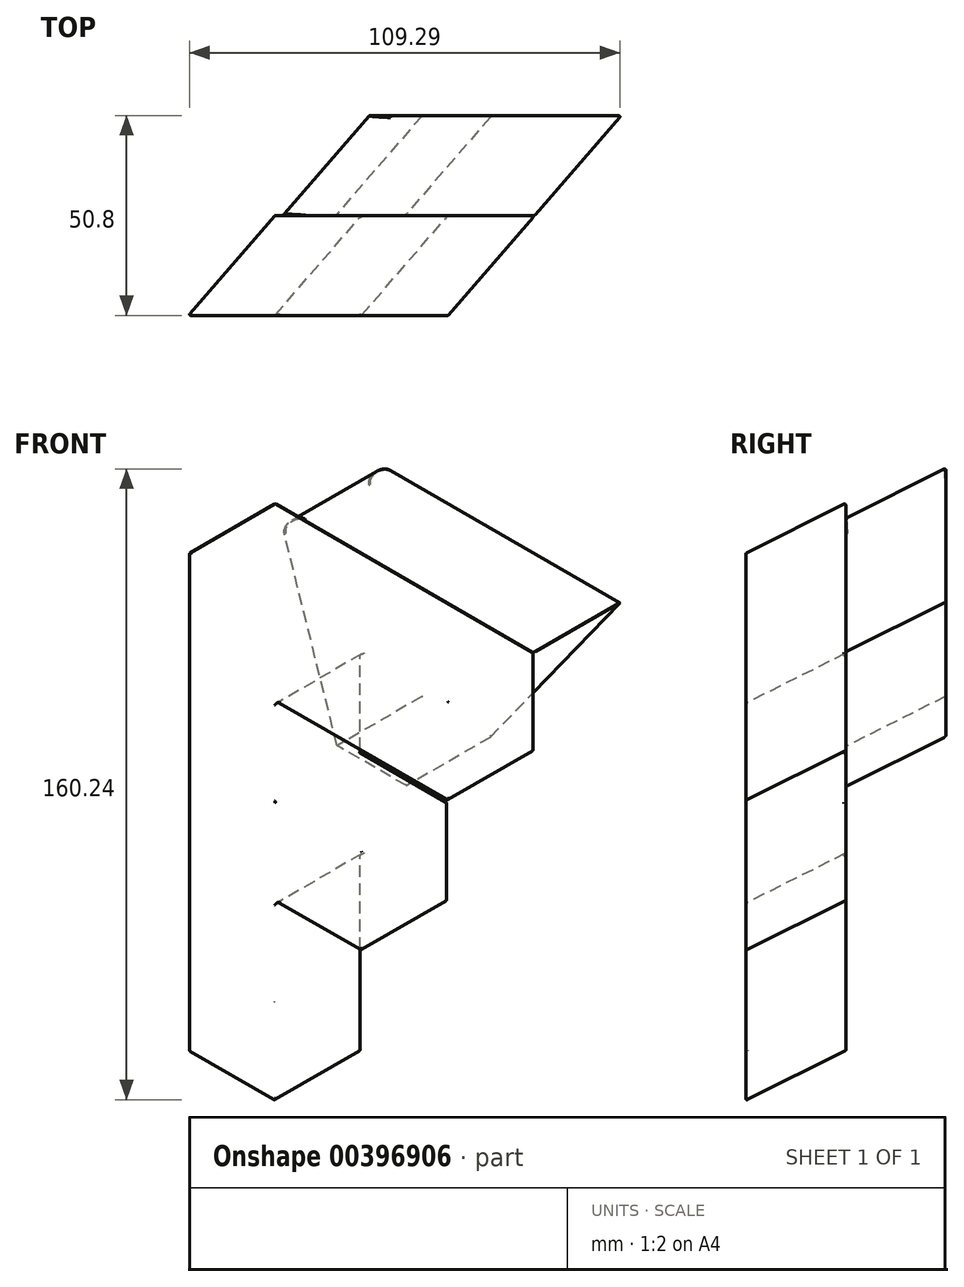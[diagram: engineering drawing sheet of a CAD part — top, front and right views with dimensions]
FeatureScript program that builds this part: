
annotation { "Feature Type Name" : "Feature", "Feature Type Description" : "" }
export const myFeature = defineFeature(function(context is Context, id is Id, definition is map)
    precondition{}
    {
        {
            var Q0;
            Q0=qCreatedBy(makeId("Front.planeOp"),FACE);
            var sketch = newSketch(context, id + "F0", { "sketchPlane" : qUnion([Q0])});
            skLineSegment(sketch, "E0", {"start": v(0, 0) * mm, "end": v(0, 127) * mm});
            skLineSegment(sketch, "E1", {"start": v(0, 127) * mm, "end": v(66, 88.9) * mm});
            skLineSegment(sketch, "E2", {"start": v(66, 88.9) * mm, "end": v(66, 63.5) * mm});
            skLineSegment(sketch, "E3", {"start": v(66, 63.5) * mm, "end": v(22, 88.9) * mm});
            skLineSegment(sketch, "E4", {"start": v(22, 88.9) * mm, "end": v(22, 63.5) * mm});
            skLineSegment(sketch, "E5", {"start": v(22, 63.5) * mm, "end": v(44, 50.8) * mm});
            skLineSegment(sketch, "E6", {"start": v(44, 50.8) * mm, "end": v(44, 25.4) * mm});
            skLineSegment(sketch, "E7", {"start": v(44, 25.4) * mm, "end": v(22, 38.1) * mm});
            skLineSegment(sketch, "E8", {"start": v(22, 38.1) * mm, "end": v(22, -12.7) * mm});
            skLineSegment(sketch, "E9", {"start": v(22, -12.7) * mm, "end": v(0, 0) * mm});
            skLineSegment(sketch, "E10", {"start": v(0, 0) * mm, "end": v(22, 12.7) * mm, "construction": true});
            skLineSegment(sketch, "E11", {"start": v(22, 12.7) * mm, "end": v(0, 25.4) * mm, "construction": true});
            skLineSegment(sketch, "E12", {"start": v(0, 25.4) * mm, "end": v(22, 38.1) * mm, "construction": true});
            skLineSegment(sketch, "E13", {"start": v(22, 38.1) * mm, "end": v(0, 50.8) * mm, "construction": true});
            skLineSegment(sketch, "E14", {"start": v(0, 50.8) * mm, "end": v(22, 63.5) * mm, "construction": true});
            skLineSegment(sketch, "E15", {"start": v(22, 63.5) * mm, "end": v(0, 76.2) * mm, "construction": true});
            skLineSegment(sketch, "E16", {"start": v(0, 76.2) * mm, "end": v(22, 88.9) * mm, "construction": true});
            skLineSegment(sketch, "E17", {"start": v(22, 88.9) * mm, "end": v(0, 101.6) * mm, "construction": true});
            skLineSegment(sketch, "E18", {"start": v(0, 101.6) * mm, "end": v(22, 114.3) * mm, "construction": true});
            skLineSegment(sketch, "E19", {"start": v(22, 38.1) * mm, "end": v(44, 50.8) * mm, "construction": true});
            skLineSegment(sketch, "E20", {"start": v(22, 88.9) * mm, "end": v(44, 101.6) * mm, "construction": true});
            skLineSegment(sketch, "E21", {"start": v(44, 101.6) * mm, "end": v(44, 76.2) * mm, "construction": true});
            skLineSegment(sketch, "E22", {"start": v(44, 76.2) * mm, "end": v(66, 88.9) * mm, "construction": true});
            skLineSegment(sketch, "E23", {"start": v(44, 76.2) * mm, "end": v(22, 63.5) * mm, "construction": true});
            skLineSegment(sketch, "E24", {"start": v(44, 50.8) * mm, "end": v(66, 63.5) * mm, "construction": true});
            skLineSegment(sketch, "E25", {"start": v(44, 25.4) * mm, "end": v(66, 38.1) * mm, "construction": true});
            skLineSegment(sketch, "E26", {"start": v(66, 38.1) * mm, "end": v(66, 63.5) * mm, "construction": true});
            skLineSegment(sketch, "E27", {"start": v(66, 63.5) * mm, "end": v(87.99, 76.2) * mm, "construction": true});
            skLineSegment(sketch, "E28", {"start": v(66, 88.9) * mm, "end": v(87.99, 101.6) * mm, "construction": true});
            skLineSegment(sketch, "E29", {"start": v(87.99, 101.6) * mm, "end": v(87.99, 76.2) * mm, "construction": true});
            skLineSegment(sketch, "E30", {"start": v(87.99, 101.6) * mm, "end": v(22, 139.7) * mm, "construction": true});
            skLineSegment(sketch, "E31", {"start": v(22, 139.7) * mm, "end": v(0, 127) * mm, "construction": true});
            skLineSegment(sketch, "E32", {"start": v(44, 25.4) * mm, "end": v(44, 0) * mm, "construction": true});
            skLineSegment(sketch, "E33", {"start": v(44, 0) * mm, "end": v(22, -12.7) * mm, "construction": true});
            skLineSegment(sketch, "E34", {"start": v(22, 114.3) * mm, "end": v(44, 127) * mm, "construction": true});
            skLineSegment(sketch, "E35", {"start": v(44, 127) * mm, "end": v(44, 101.6) * mm, "construction": true});
            skLineSegment(sketch, "E36", {"start": v(44, 101.6) * mm, "end": v(66, 114.3) * mm, "construction": true});
            skLineSegment(sketch, "E37", {"start": v(66, 114.3) * mm, "end": v(66, 88.9) * mm, "construction": true});
            skLineSegment(sketch, "E38", {"start": v(44, 76.2) * mm, "end": v(44, 50.8) * mm, "construction": true});
            skLineSegment(sketch, "E39", {"start": v(22, 63.5) * mm, "end": v(22, 38.1) * mm, "construction": true});
            skLineSegment(sketch, "E40", {"start": v(22, 12.7) * mm, "end": v(44, 25.4) * mm, "construction": true});
            skLineSegment(sketch, "E41", {"start": v(22, 12.7) * mm, "end": v(44, 0) * mm, "construction": true});
            skLineSegment(sketch, "E42", {"start": v(22, 139.7) * mm, "end": v(22, 114.3) * mm, "construction": true});
            skLineSegment(sketch, "E43", {"start": v(44, 50.8) * mm, "end": v(66, 38.1) * mm, "construction": true});
            skLineSegment(sketch, "E44", {"start": v(66, 88.9) * mm, "end": v(87.99, 76.2) * mm, "construction": true});
            skSolve(sketch);
        }
        {
            var Q0;
            Q0=qCreatedBy(makeId("Front.planeOp"),FACE);
            cPlane(context, id + "F1", {"entities" : qUnion([Q0]), "cplaneType" : CPlaneType.OFFSET, "offset" : 25.4 * mm, "oppositeDirection" : true, "width" : 152.4 * mm, "height" : 152.4 * mm});
        }
        {
            var Q0;
            Q0=qCreatedBy(id+"F1.planeOp",FACE);
            var sketch = newSketch(context, id + "F2", { "sketchPlane" : qUnion([Q0])});
            skLineSegment(sketch, "E45", {"start": v(22, 12.7) * mm, "end": v(22, 139.7) * mm});
            skLineSegment(sketch, "E46", {"start": v(22, 139.7) * mm, "end": v(87.99, 101.6) * mm});
            skLineSegment(sketch, "E47", {"start": v(87.99, 101.6) * mm, "end": v(87.99, 76.2) * mm});
            skLineSegment(sketch, "E48", {"start": v(87.99, 76.2) * mm, "end": v(44, 101.6) * mm});
            skLineSegment(sketch, "E49", {"start": v(44, 101.6) * mm, "end": v(44, 76.2) * mm});
            skLineSegment(sketch, "E50", {"start": v(44, 76.2) * mm, "end": v(66, 63.5) * mm});
            skLineSegment(sketch, "E51", {"start": v(66, 63.5) * mm, "end": v(66, 38.1) * mm});
            skLineSegment(sketch, "E52", {"start": v(66, 38.1) * mm, "end": v(44, 50.8) * mm});
            skLineSegment(sketch, "E53", {"start": v(44, 50.8) * mm, "end": v(44, 0) * mm});
            skLineSegment(sketch, "E54", {"start": v(44, 0) * mm, "end": v(22, 12.7) * mm});
            skSolve(sketch);
        }
        {
            var Q0;
            Q0=makeQuery(id+"F0.imprint","IMPRINT",FACE,{"disambiguationData":[TD([[makeQuery(id+"F0.imprint","IMPRINT",EDGE,{"derivedFrom":sQuery(id+"F0.wireOp",EDGE,"E0")}),-1.0]])]});
            var Q1;
            Q1=makeQuery(id+"F2.imprint","IMPRINT",FACE,{"disambiguationData":[TD([[makeQuery(id+"F2.imprint","IMPRINT",EDGE,{"derivedFrom":sQuery(id+"F2.wireOp",EDGE,"E45")}),-1.0]])]});
            loft(context, id + "F3", {"sheetProfilesArray" : [{ "sheetProfileEntities" : qUnion([Q0]) }, { "sheetProfileEntities" : qUnion([Q1]) }]});
        }
        {
            var Q0;
            Q0=makeQuery(id+"F3.opLoft","MID_CAP_EDGE",EDGE,{"disambiguationData":[OSD([sQuery(id+"F2.wireOp",EDGE,"E45"),sQuery(id+"F2.wireOp",EDGE,"E46"),sQuery(id+"F2.wireOp",EDGE,"E47")])],"capPos":1.0});
            cPlane(context, id + "F4", {"entities" : qUnion([Q0]), "cplaneType" : CPlaneType.LINE_ANGLE, "offset" : 25.4 * mm, "angle" : 67.3 * degree, "oppositeDirection" : true, "width" : 152.4 * mm, "height" : 152.4 * mm});
        }
        {
            var Q0;
            Q0=makeQuery(id+"F3.opLoft","SWEPT_EDGE",EDGE,{"disambiguationData":[OSD([sQuery(id+"F0.wireOp",EDGE,"E1"),sQuery(id+"F0.wireOp",EDGE,"E2"),sQuery(id+"F2.wireOp",EDGE,"E46"),sQuery(id+"F2.wireOp",EDGE,"E47")])]});
            var Q1;
            Q1=makeQuery(id+"F3.opLoft","MID_CAP_VERTEX",VERTEX,{"disambiguationData":[OSD([sQuery(id+"F2.wireOp",EDGE,"E45"),sQuery(id+"F2.wireOp",EDGE,"E46")])],"capPos":1.0});
            cPlane(context, id + "F5", {"entities" : qUnion([Q0, Q1]), "cplaneType" : CPlaneType.LINE_POINT, "offset" : 25.4 * mm, "width" : 152.4 * mm, "height" : 152.4 * mm});
        }
        {
            var Q0;
            Q0=qCreatedBy(id+"F5.planeOp",FACE);
            var sketch = newSketch(context, id + "F6", { "sketchPlane" : qUnion([Q0])});
            skLineSegment(sketch, "E55.bottom", {"start": v(-27.82, 79.51) * mm, "end": v(34.78, 113.6) * mm});
            skLineSegment(sketch, "E55.top", {"start": v(-5.1, 37.78) * mm, "end": v(57.5, 71.86) * mm});
            skLineSegment(sketch, "E55.left", {"start": v(-27.82, 79.51) * mm, "end": v(-5.1, 37.78) * mm, "construction": true});
            skLineSegment(sketch, "E55.right", {"start": v(34.78, 113.6) * mm, "end": v(57.5, 71.86) * mm, "construction": true});
            skLineSegment(sketch, "E56", {"start": v(-5.1, 37.78) * mm, "end": v(34.78, 113.6) * mm, "construction": true});
            skLineSegment(sketch, "E57.top", {"start": v(17.61, -3.96) * mm, "end": v(80.22, 30.12) * mm, "construction": true});
            skLineSegment(sketch, "E57.left", {"start": v(-5.1, 37.78) * mm, "end": v(17.61, -3.96) * mm});
            skLineSegment(sketch, "E57.right", {"start": v(57.5, 71.86) * mm, "end": v(80.22, 30.12) * mm, "construction": true});
            skLineSegment(sketch, "E58", {"start": v(17.61, -3.96) * mm, "end": v(57.5, 71.86) * mm});
            skLineSegment(sketch, "E59", {"start": v(-11.18, 48.93) * mm, "end": v(5.55, 58.04) * mm});
            skLineSegment(sketch, "E60", {"start": v(5.55, 58.04) * mm, "end": v(34.78, 113.6) * mm});
            skLineSegment(sketch, "E61", {"start": v(-11.18, 48.93) * mm, "end": v(-27.82, 79.51) * mm});
            skSolve(sketch);
        }
        {
            var Q0;
            Q0=makeQuery(id+"F3.opLoft","CAP_FACE",FACE,{"disambiguationData":[OSD([makeQuery(id+"F0.imprint","IMPRINT",FACE,{"disambiguationData":[TD([[makeQuery(id+"F0.imprint","IMPRINT",EDGE,{"derivedFrom":sQuery(id+"F0.wireOp",EDGE,"E0")}),-1.0]])]})])],"isStart":true});
            var Q1;
            Q1=makeQuery(id+"F3.opLoft","CAP_FACE",FACE,{"disambiguationData":[OSD([makeQuery(id+"F2.imprint","IMPRINT",FACE,{"disambiguationData":[TD([[makeQuery(id+"F2.imprint","IMPRINT",EDGE,{"derivedFrom":sQuery(id+"F2.wireOp",EDGE,"E45")}),-1.0]])]})])],"isStart":true});
            var Q2;
            Q2=makeQuery(id+"F3.opLoft","SWEPT_FACE",FACE,{"disambiguationData":[OSD([sQuery(id+"F0.wireOp",EDGE,"E3"),sQuery(id+"F0.wireOp",EDGE,"E4"),sQuery(id+"F0.wireOp",EDGE,"E5"),sQuery(id+"F2.wireOp",EDGE,"E48"),sQuery(id+"F2.wireOp",EDGE,"E49"),sQuery(id+"F2.wireOp",EDGE,"E50")])]});
            var Q3;
            Q3=makeQuery(id+"F3.opLoft","SWEPT_FACE",FACE,{"disambiguationData":[OSD([sQuery(id+"F0.wireOp",EDGE,"E2"),sQuery(id+"F0.wireOp",EDGE,"E3"),sQuery(id+"F0.wireOp",EDGE,"E4"),sQuery(id+"F2.wireOp",EDGE,"E47"),sQuery(id+"F2.wireOp",EDGE,"E48"),sQuery(id+"F2.wireOp",EDGE,"E49")])]});
            var Q4;
            Q4=makeQuery(id+"F3.opLoft","SWEPT_FACE",FACE,{"disambiguationData":[OSD([sQuery(id+"F0.wireOp",EDGE,"E4"),sQuery(id+"F0.wireOp",EDGE,"E5"),sQuery(id+"F0.wireOp",EDGE,"E6"),sQuery(id+"F2.wireOp",EDGE,"E49"),sQuery(id+"F2.wireOp",EDGE,"E50"),sQuery(id+"F2.wireOp",EDGE,"E51")])]});
            var Q5;
            Q5=makeQuery(id+"F3.opLoft","SWEPT_FACE",FACE,{"disambiguationData":[OSD([sQuery(id+"F0.wireOp",EDGE,"E5"),sQuery(id+"F0.wireOp",EDGE,"E6"),sQuery(id+"F0.wireOp",EDGE,"E7"),sQuery(id+"F2.wireOp",EDGE,"E50"),sQuery(id+"F2.wireOp",EDGE,"E51"),sQuery(id+"F2.wireOp",EDGE,"E52")])]});
            var Q6;
            Q6=makeQuery(id+"F3.opLoft","SWEPT_FACE",FACE,{"disambiguationData":[OSD([sQuery(id+"F0.wireOp",EDGE,"E7"),sQuery(id+"F0.wireOp",EDGE,"E8"),sQuery(id+"F0.wireOp",EDGE,"E9"),sQuery(id+"F2.wireOp",EDGE,"E52"),sQuery(id+"F2.wireOp",EDGE,"E53"),sQuery(id+"F2.wireOp",EDGE,"E54")])]});
            var Q7;
            Q7=makeQuery(id+"F3.opLoft","SWEPT_FACE",FACE,{"disambiguationData":[OSD([sQuery(id+"F0.wireOp",EDGE,"E1"),sQuery(id+"F0.wireOp",EDGE,"E2"),sQuery(id+"F0.wireOp",EDGE,"E3"),sQuery(id+"F2.wireOp",EDGE,"E46"),sQuery(id+"F2.wireOp",EDGE,"E47"),sQuery(id+"F2.wireOp",EDGE,"E48")])]});
            var Q8;
            Q8=makeQuery(id+"F3.opLoft","SWEPT_FACE",FACE,{"disambiguationData":[OSD([sQuery(id+"F0.wireOp",EDGE,"E0"),sQuery(id+"F0.wireOp",EDGE,"E1"),sQuery(id+"F0.wireOp",EDGE,"E2"),sQuery(id+"F2.wireOp",EDGE,"E45"),sQuery(id+"F2.wireOp",EDGE,"E46"),sQuery(id+"F2.wireOp",EDGE,"E47")])]});
            var Q9;
            Q9=makeQuery(id+"F3.opLoft","SWEPT_FACE",FACE,{"disambiguationData":[OSD([sQuery(id+"F0.wireOp",EDGE,"E0"),sQuery(id+"F0.wireOp",EDGE,"E8"),sQuery(id+"F0.wireOp",EDGE,"E9"),sQuery(id+"F2.wireOp",EDGE,"E45"),sQuery(id+"F2.wireOp",EDGE,"E53"),sQuery(id+"F2.wireOp",EDGE,"E54")])]});
            var Q10;
            Q10=makeQuery(id+"F3.opLoft","SWEPT_FACE",FACE,{"disambiguationData":[OSD([sQuery(id+"F0.wireOp",EDGE,"E0"),sQuery(id+"F0.wireOp",EDGE,"E1"),sQuery(id+"F0.wireOp",EDGE,"E9"),sQuery(id+"F2.wireOp",EDGE,"E45"),sQuery(id+"F2.wireOp",EDGE,"E46"),sQuery(id+"F2.wireOp",EDGE,"E54")])]});
            fillet(context, id + "F7", {"entities" : qUnion([Q0, Q1, Q2, Q3, Q4, Q5, Q6, Q7, Q8, Q9, Q10]), "radius" : .3 * mm, "tangentPropagation" : true, "allowEdgeOverflow" : false});
        }
        {
            var Q0;
            Q0=qCreatedBy(id+"F1.planeOp",FACE);
            cPlane(context, id + "F8", {"entities" : qUnion([Q0]), "cplaneType" : CPlaneType.OFFSET, "offset" : 25.4 * mm, "oppositeDirection" : true, "width" : 152.4 * mm, "height" : 152.4 * mm});
        }
        {
            var Q0;
            Q0=makeQuery(id+"F6.imprint","IMPRINT",FACE,{"disambiguationData":[TD([[makeQuery(id+"F6.imprint","IMPRINT",EDGE,{"derivedFrom":sQuery(id+"F6.wireOp",EDGE,"E55.bottom")}),-1.0]])]});
            var Q1;
            Q1=makeQuery(id+"F6.imprint","IMPRINT",FACE,{"disambiguationData":[TD([[makeQuery(id+"F6.imprint","IMPRINT",EDGE,{"derivedFrom":sQuery(id+"F6.wireOp",EDGE,"E55.top")}),-1.0]])]});
            var Q2;
            Q2=qCreatedBy(id+"F8.planeOp",FACE);
            var Q3;
            Q3=makeQuery(id+"F3.opLoft","CAP_FACE",FACE,{"disambiguationData":[OSD([makeQuery(id+"F2.imprint","IMPRINT",FACE,{"disambiguationData":[TD([[makeQuery(id+"F2.imprint","IMPRINT",EDGE,{"derivedFrom":sQuery(id+"F2.wireOp",EDGE,"E45")}),-1.0]])]})])],"isStart":true});
            extrude(context, id + "F9", {"entities" : qUnion([Q0, Q1]), "endBound" : BoundingType.UP_TO_SURFACE, "endBoundEntityFace" : qUnion([Q2]), "depth" : 25.4 * mm, "hasSecondDirection" : true, "secondDirectionBound" : SecondDirectionBoundingType.UP_TO_SURFACE, "secondDirectionOppositeDirection" : true, "secondDirectionBoundEntityFace" : qUnion([Q3]), "secondDirectionDepth" : 25.4 * mm});
        }
        {
            var Q0;
            Q0=makeQuery(id+"F9.opExtrude","SWEPT_EDGE",EDGE,{"disambiguationData":[OSD([sQuery(id+"F6.wireOp",EDGE,"E55.bottom"),sQuery(id+"F6.wireOp",EDGE,"E60")])]});
            var Q1;
            Q1=makeQuery(id+"F9.opExtrude","TWEAK_EDGE",EDGE,{"derivedFrom":[makeQuery(id+"F6.imprint","IMPRINT",EDGE,{"derivedFrom":sQuery(id+"F6.wireOp",EDGE,"E55.bottom")}),makeQuery(id+"F6.imprint","IMPRINT",EDGE,{"derivedFrom":sQuery(id+"F6.wireOp",EDGE,"E61")})]});
            var Q2;
            Q2=makeQuery(id+"F9.opExtrude","TWEAK_EDGE",EDGE,{"derivedFrom":[makeQuery(id+"F6.imprint","IMPRINT",EDGE,{"derivedFrom":sQuery(id+"F6.wireOp",EDGE,"E59")}),makeQuery(id+"F6.imprint","IMPRINT",EDGE,{"derivedFrom":sQuery(id+"F6.wireOp",EDGE,"E61")})]});
            var Q3;
            Q3=makeQuery(id+"F9.opExtrude","TWEAK_EDGE",EDGE,{"derivedFrom":[makeQuery(id+"F6.imprint","IMPRINT",EDGE,{"derivedFrom":sQuery(id+"F6.wireOp",EDGE,"E59")}),makeQuery(id+"F6.imprint","IMPRINT",EDGE,{"derivedFrom":sQuery(id+"F6.wireOp",EDGE,"E60")})]});
            var Q4;
            Q4=makeQuery(id+"F9.opExtrude","TWEAK_EDGE",EDGE,{"derivedFrom":[makeQuery(id+"F6.imprint","IMPRINT",EDGE,{"derivedFrom":sQuery(id+"F6.wireOp",EDGE,"E55.top")}),makeQuery(id+"F6.imprint","IMPRINT",EDGE,{"derivedFrom":sQuery(id+"F6.wireOp",EDGE,"E57.left")})]});
            var Q5;
            Q5=makeQuery(id+"F9.opExtrude","TWEAK_EDGE",EDGE,{"derivedFrom":[makeQuery(id+"F6.imprint","IMPRINT",EDGE,{"derivedFrom":sQuery(id+"F6.wireOp",EDGE,"E55.top")}),makeQuery(id+"F6.imprint","IMPRINT",EDGE,{"derivedFrom":sQuery(id+"F6.wireOp",EDGE,"E58")})]});
            var Q6;
            Q6=makeQuery(id+"F9.opExtrude","TWEAK_EDGE",EDGE,{"derivedFrom":[makeQuery(id+"F6.imprint","IMPRINT",EDGE,{"derivedFrom":sQuery(id+"F6.wireOp",EDGE,"E57.left")}),makeQuery(id+"F6.imprint","IMPRINT",EDGE,{"derivedFrom":sQuery(id+"F6.wireOp",EDGE,"E58")})]});
            fillet(context, id + "F10", {"entities" : qUnion([Q0, Q1, Q2, Q3, Q4, Q5, Q6]), "radius" : 2.54 * mm, "tangentPropagation" : true, "allowEdgeOverflow" : false});
        }
        {
            var Q0;
            {var subQ0=dummyQuery(id+"F8.planeOp",FACE);Q0=qUnion([makeQuery(id+"F9.opExtrude","CAP_FACE",FACE,{"disambiguationData":[OSD([sQuery(id+"F6.wireOp",EDGE,"E55.bottom"),sQuery(id+"F6.wireOp",EDGE,"E59"),sQuery(id+"F6.wireOp",EDGE,"E60"),sQuery(id+"F6.wireOp",EDGE,"E61")]),topologyDisambiguationEdgeConnected([subQ0])],"isStart":false}),makeQuery(id+"F9.opExtrude","CAP_FACE",FACE,{"disambiguationData":[OSD([sQuery(id+"F6.wireOp",EDGE,"E55.top"),sQuery(id+"F6.wireOp",EDGE,"E57.left"),sQuery(id+"F6.wireOp",EDGE,"E58")]),topologyDisambiguationEdgeConnected([subQ0])],"isStart":false})]);}
            var Q1;
            {var subQ0=dummyQuery(id+"F8.planeOp",FACE);Q1=qUnion([makeQuery(id+"F9.opExtrude","CAP_FACE",FACE,{"disambiguationData":[OSD([sQuery(id+"F6.wireOp",EDGE,"E55.bottom"),sQuery(id+"F6.wireOp",EDGE,"E59"),sQuery(id+"F6.wireOp",EDGE,"E60"),sQuery(id+"F6.wireOp",EDGE,"E61")]),topologyDisambiguationEdgeConnected([subQ0])],"isStart":false}),makeQuery(id+"F9.opExtrude","CAP_FACE",FACE,{"disambiguationData":[OSD([sQuery(id+"F6.wireOp",EDGE,"E55.top"),sQuery(id+"F6.wireOp",EDGE,"E57.left"),sQuery(id+"F6.wireOp",EDGE,"E58")]),topologyDisambiguationEdgeConnected([subQ0])],"isStart":false})]);}
            var Q2;
            {var subQ0=makeQuery(id+"F3.opLoft","CAP_FACE",FACE,{"disambiguationData":[OSD([makeQuery(id+"F2.imprint","IMPRINT",FACE,{"disambiguationData":[TD([[makeQuery(id+"F2.imprint","IMPRINT",EDGE,{"derivedFrom":sQuery(id+"F2.wireOp",EDGE,"E45")}),-1.0]])]})])],"isStart":true});Q2=qUnion([makeQuery(id+"F9.opExtrude","CAP_FACE",FACE,{"disambiguationData":[OSD([sQuery(id+"F6.wireOp",EDGE,"E55.bottom"),sQuery(id+"F6.wireOp",EDGE,"E59"),sQuery(id+"F6.wireOp",EDGE,"E60"),sQuery(id+"F6.wireOp",EDGE,"E61")]),topologyDisambiguationEdgeConnected([subQ0])],"isStart":false}),makeQuery(id+"F9.opExtrude","CAP_FACE",FACE,{"disambiguationData":[OSD([sQuery(id+"F6.wireOp",EDGE,"E55.top"),sQuery(id+"F6.wireOp",EDGE,"E57.left"),sQuery(id+"F6.wireOp",EDGE,"E58")]),topologyDisambiguationEdgeConnected([subQ0])],"isStart":false})]);}
            var Q3;
            {var subQ0=makeQuery(id+"F3.opLoft","CAP_FACE",FACE,{"disambiguationData":[OSD([makeQuery(id+"F2.imprint","IMPRINT",FACE,{"disambiguationData":[TD([[makeQuery(id+"F2.imprint","IMPRINT",EDGE,{"derivedFrom":sQuery(id+"F2.wireOp",EDGE,"E45")}),-1.0]])]})])],"isStart":true});Q3=qUnion([makeQuery(id+"F9.opExtrude","CAP_FACE",FACE,{"disambiguationData":[OSD([sQuery(id+"F6.wireOp",EDGE,"E55.bottom"),sQuery(id+"F6.wireOp",EDGE,"E59"),sQuery(id+"F6.wireOp",EDGE,"E60"),sQuery(id+"F6.wireOp",EDGE,"E61")]),topologyDisambiguationEdgeConnected([subQ0])],"isStart":false}),makeQuery(id+"F9.opExtrude","CAP_FACE",FACE,{"disambiguationData":[OSD([sQuery(id+"F6.wireOp",EDGE,"E55.top"),sQuery(id+"F6.wireOp",EDGE,"E57.left"),sQuery(id+"F6.wireOp",EDGE,"E58")]),topologyDisambiguationEdgeConnected([subQ0])],"isStart":false})]);}
            fillet(context, id + "F11", {"entities" : qUnion([Q0, Q1, Q2, Q3]), "radius" : .3 * mm, "tangentPropagation" : true, "allowEdgeOverflow" : false});
        }
    });
